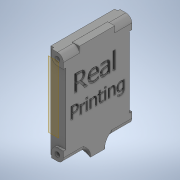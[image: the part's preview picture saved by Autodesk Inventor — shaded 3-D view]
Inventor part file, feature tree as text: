
AUTODESK INVENTOR PART (.ipt)
format: ipt  version: 2022 (Build 260153000, 153)  size: 547,840 bytes
history: native  units: mm
features: sketch x9, reference x9, extrude x8, other x7, plane x1, mirror x1, chamfer x1, fillet x1
ambient origin geometry x8: Origin, YZ Plane, XZ Plane, XY Plane, X Axis, Y Axis, Z Axis, Center Point
bodies: Solid1 (feature_tree)
feature tree (37):
  extrude  "Extrusion1"  Depth=27.0mm
  plane  "Work Plane1"
  extrude  "Extrusion2"  Depth=1.0mm
  extrude  "Extrusion3"  Depth=4.5mm TaperAngle=0.0deg
  sketch  "Sketch4"  dims[d18=14.5mm d19=0.0mm d20=135.0deg]
  extrude  "Extrusion4"  TaperAngle=135.0deg  [1 undecoded]
  mirror  "Mirror2"
  extrude  "Extrusion5"  Depth=30.0mm TaperAngle=0.0deg
  extrude  "Extrusion6"  Depth=6.0mm TaperAngle=0.0deg
  extrude  "Extrusion8"  Depth=3.0mm
  chamfer  "Chamfer1"  Distance=8.530296mm
  fillet  "Fillet1"  Radius=11.80564mm
  extrude  "Extrusion9"  Depth=1.0mm TaperAngle=0.0deg
  sketch  "Sketch1"  dims[d0=25.5mm d1=27.0mm]
  sketch  "Sketch2"  dims[d9=6.25mm d10=0.0mm d13=1.0mm]
  reference  "Reference1"
  sketch  "Sketch3"  dims[d14=14.5mm d15=0.0mm d16=4.5mm d17=0.0mm]
  reference  "Reference2"
  reference  "Reference3"
  sketch  "Sketch5"  dims[d21=3.0mm d22=0.0mm d23=30.0mm d24=0.0mm]
  reference  "Reference4"
  reference  "Reference5"
  reference  "Reference6"
  sketch  "Sketch6"  dims[d31=6.0mm d32=6.0mm d33=0.0mm]
  sketch  "Sketch7"  dims[d34=6.0mm d35=3.0mm d36=45.0deg d37=3.0mm]
  reference  "Reference8"
  reference  "Reference14"
  reference  "Reference15"
  sketch  "Sketch9"  dims[d42=17.060591mm]
  sketch  "Sketch10"  dims[d43=23.611281mm d44=8.530296mm d45=11.80564mm d46=1.0mm d47=0.0mm]
  other  "Volcano_Printhead.iam"
  other  "4010 turbo fan v3:3"
  other  "sherpa_mini_release1:1"
  other  "Assembly246"
  other  "4010 turbo fan v3:2"
  other  "Assembly1"
  other  "v6_Clamp V2:1"
note: 1 required parameter value undecoded (feature->parameter linkage not recoverable at this tier; creation-order binding heuristic only, values carry confidence <= 0.55)
